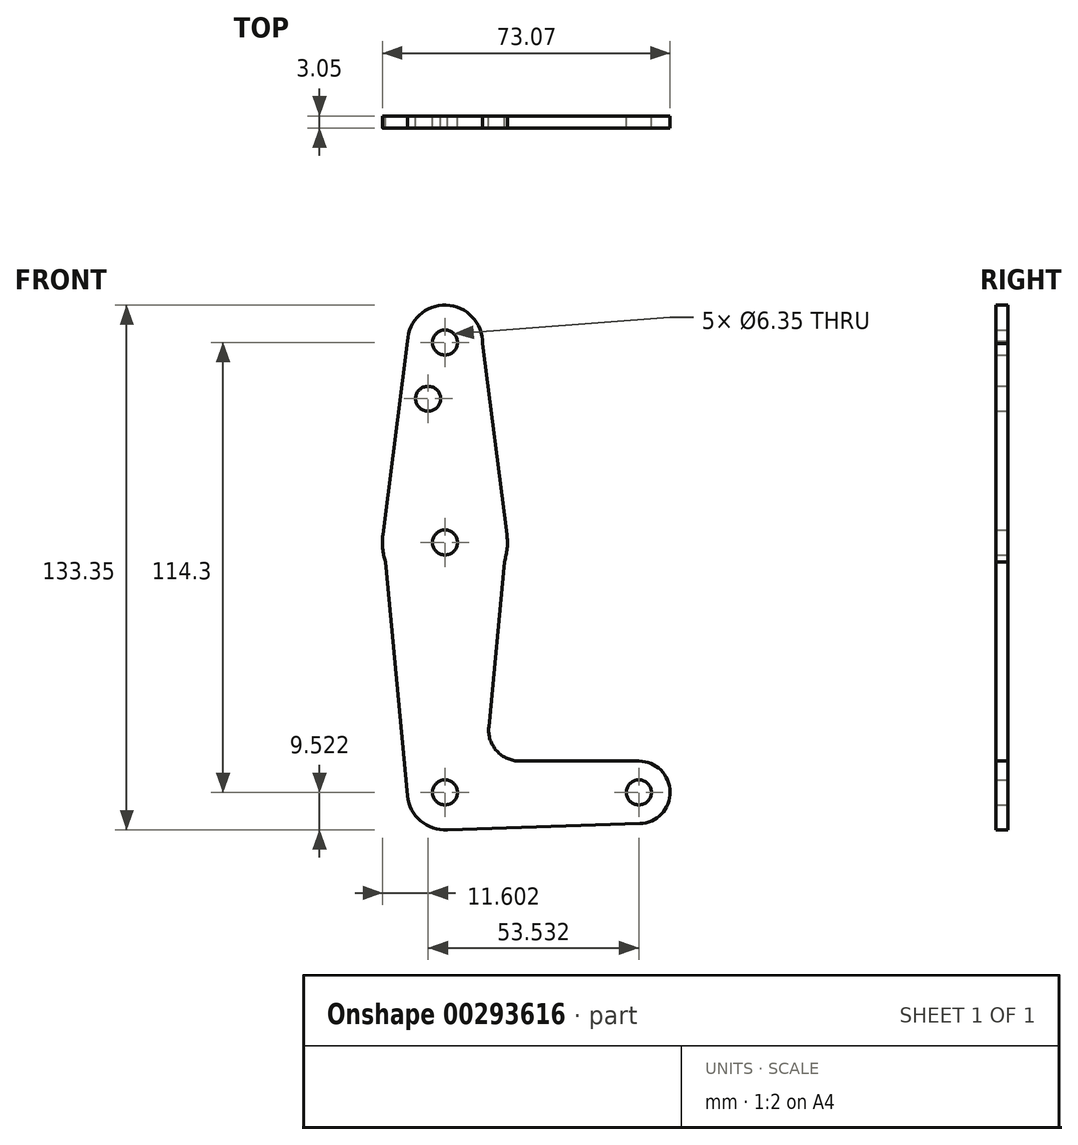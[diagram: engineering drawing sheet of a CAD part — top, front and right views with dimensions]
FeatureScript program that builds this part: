
annotation { "Feature Type Name" : "Feature", "Feature Type Description" : "" }
export const myFeature = defineFeature(function(context is Context, id is Id, definition is map)
    precondition{}
    {
        {
            var Q0;
            Q0=qCreatedBy(makeId("Front.planeOp"),FACE);
            var sketch = newSketch(context, id + "F0", { "sketchPlane" : qUnion([Q0])});
            skLineSegment(sketch, "E0", {"start": v(-32.77, 64.22) * mm, "end": v(-32.77, -50.08) * mm, "construction": true});
            skLineSegment(sketch, "E1", {"start": v(-32.77, -50.08) * mm, "end": v(16.5, -50.08) * mm, "construction": true});
            skCircle(sketch, "E2", {"center": v(-32.77, 64.22) * mm, "radius": 9.53 * mm});
            skCircle(sketch, "E3", {"center": v(-32.77, -50.08) * mm, "radius": 9.53 * mm});
            skCircle(sketch, "E4", {"center": v(16.5, -50.08) * mm, "radius": 7.94 * mm});
            skCircle(sketch, "E5", {"center": v(-32.77, 13.42) * mm, "radius": 15.88 * mm});
            skLineSegment(sketch, "E6", {"start": v(-42.29, 64.56) * mm, "end": v(-48.52, 15.42) * mm});
            skLineSegment(sketch, "E7", {"start": v(-23.25, 63.94) * mm, "end": v(-17.02, 15.44) * mm});
            skLineSegment(sketch, "E8", {"start": v(-48.52, 15.42) * mm, "end": v(-42.25, -50.97) * mm});
            skLineSegment(sketch, "E9", {"start": v(-17.02, 15.44) * mm, "end": v(-21.63, -33.44) * mm});
            skLineSegment(sketch, "E10", {"start": v(-32.77, -59.6) * mm, "end": v(16.75, -58.01) * mm});
            skLineSegment(sketch, "E11", {"start": v(16.5, -42.14) * mm, "end": v(-13.72, -42.14) * mm});
            skPoint(sketch, "E12.start.orphan", {"position": v(-45.4, 39.99) * mm});
            skCircle(sketch, "E13", {"center": v(-32.77, 64.22) * mm, "radius": 3.18 * mm});
            skCircle(sketch, "E14", {"center": v(-32.77, 13.42) * mm, "radius": 3.18 * mm});
            skCircle(sketch, "E15", {"center": v(-32.77, -50.08) * mm, "radius": 3.18 * mm});
            skCircle(sketch, "E16", {"center": v(16.5, -50.08) * mm, "radius": 3.18 * mm});
            skCircle(sketch, "E17", {"center": v(-37.04, 49.95) * mm, "radius": 3.18 * mm});
            skArc(sketch, "E18.filletArc", {"start": v(-21.63, -33.44) * mm, "mid": v(-19.6, -39.54) * mm, "end": v(-13.72, -42.14) * mm});
            skSolve(sketch);
        }
        {
            var Q0;
            Q0 = qSketchRegion(id + "F0", true);
            extrude(context, id + "F1", {"entities" : qUnion([Q0]), "depth" : 3.05 * mm});
        }
    });
